# Revit family: O3.25EM-NRG_11BF
name_source: partatom
category: Mechanical Equipment
revit_build: Autodesk Revit 2017 (Build: 20171027_0315(x64)
units: mm (PartAtom-declared; Revit-internal decimal feet)

## family parameters
Always vertical = Yes
Cut with Voids When Loaded = No
OmniClass Number = 23.40.40.11.17
OmniClass Title = Refrigerated Cases
Part Type = Normal
Room Calculation Point = No
Round Connector Dimension = Use Radius
Shared = No
Work Plane-Based = Yes

## types (3) — shared parameters
BASE HEIGHT = 11"
CERTIFICATIONS = NSF 7, UL471, CSA
DATE = 11/25/13
DIEBOARD HEIGHT = 0"
DRAIN PIPE LENGTH = 0"
Default Elevation = 48"
Description = Multi-Deck End-Cap Merchandiser  with Synerg-E
HEIGHT = 58 1/2"
Keynote = Dairy /Deli / Meat/Produce
LEGEND NUMBER = O3.25EM-NRG
LENGTH = 87 3/4"
Manufacturer = HILL PHOENIX
Model = O3.25EM-NRG
REAR LOAD = 24"
REF PIPE LENGTH = 28 5/8"
REF PLANE FRONT BACK = 21 5/8"
REF PLANE LEFT RIGHT = 43 7/8"
SHELVE LENGTH = 48"
TOEKICK HEIGHT = 5 1/2"
TOEKICK INSET = 1 1/2"
URL = http://www.hillphoenix.com
WIDTH = 43 1/4"

## type names (no varying parameters)
- O3.25EM-NRG-11"BF
- O3.25EM-NRG-11"BF-Dairy/Deli/Produce
- O3.25EM-NRG-11"BF-Meat

## geometry (parser evidence)
native form markers: Blend x2, Sweep x10
no freeform markers — native parametric forms only
